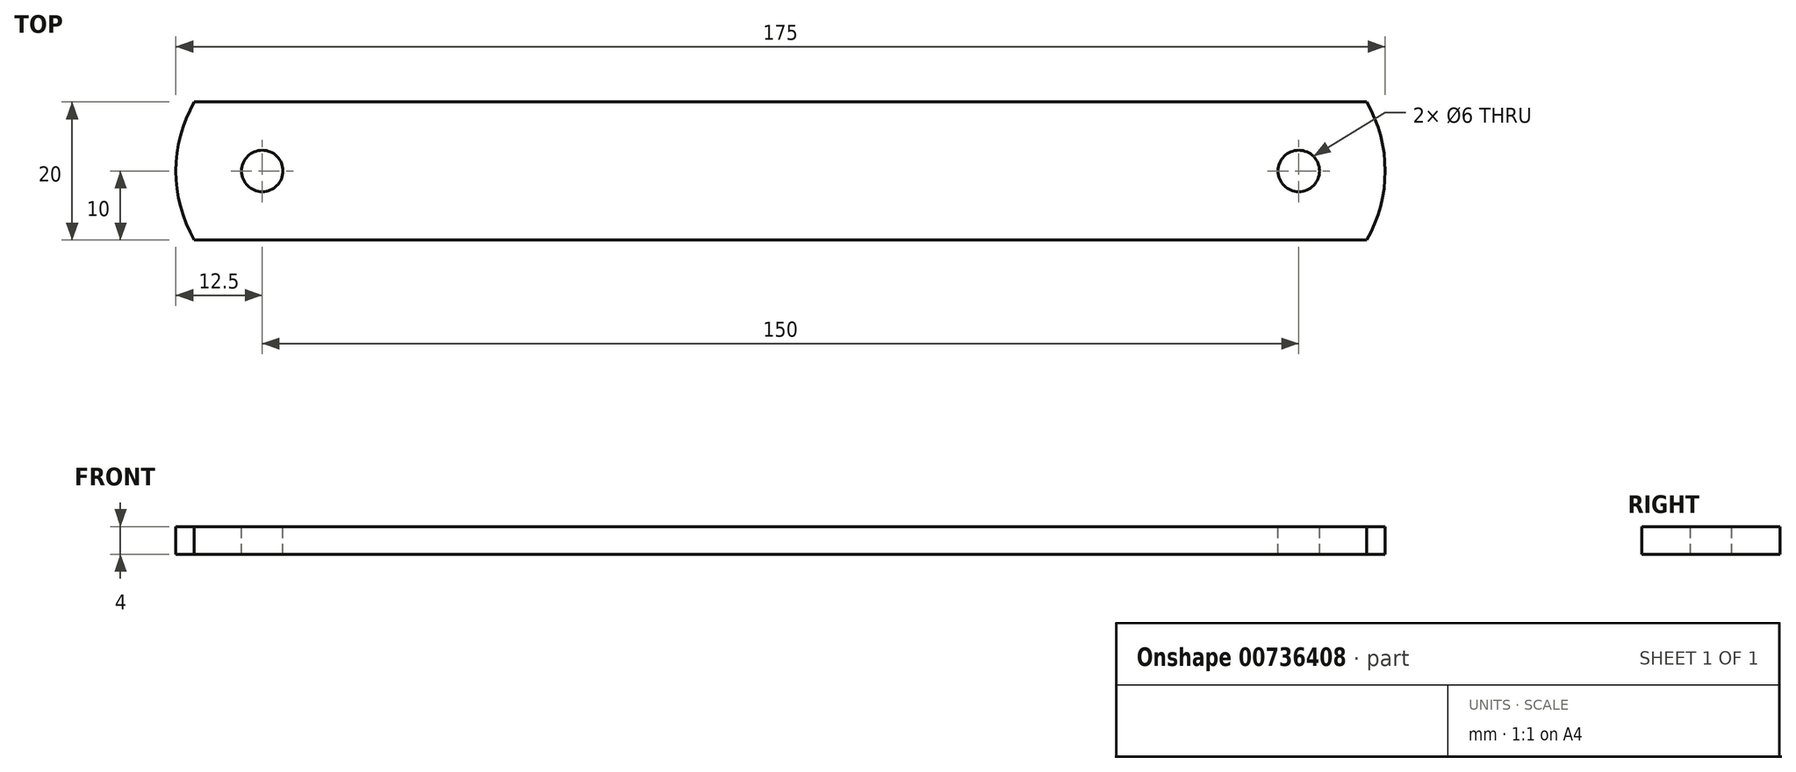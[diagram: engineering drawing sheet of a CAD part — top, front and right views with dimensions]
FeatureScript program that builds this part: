
annotation { "Feature Type Name" : "Feature", "Feature Type Description" : "" }
export const myFeature = defineFeature(function(context is Context, id is Id, definition is map)
    precondition{}
    {
        {
            var Q0;
            Q0=qCreatedBy(makeId("Top.planeOp"),FACE);
            var sketch = newSketch(context, id + "F0", { "sketchPlane" : qUnion([Q0])});
            skLineSegment(sketch, "E0.bottom", {"start": v(0, 0) * mm, "end": v(169.64, 0) * mm});
            skLineSegment(sketch, "E0.top", {"start": v(0, -20) * mm, "end": v(169.64, -20) * mm});
            skArc(sketch, "E1", {"start": v(169.64, -20) * mm, "mid": v(172.32, -10) * mm, "end": v(169.64, 0) * mm});
            skArc(sketch, "E2", {"start": v(0, 0) * mm, "mid": v(-2.68, -10) * mm, "end": v(0, -20) * mm});
            skSolve(sketch);
        }
        {
            var Q0;
            Q0=makeQuery(id+"F0.imprint","IMPRINT",FACE,{"disambiguationData":[TD([[makeQuery(id+"F0.imprint","IMPRINT",EDGE,{"derivedFrom":sQuery(id+"F0.wireOp",EDGE,"E0.bottom")}),-1.0]])]});
            extrude(context, id + "F1", {"entities" : qUnion([Q0]), "depth" : 4 * mm, "offsetDistance" : 25 * mm});
        }
        {
            var Q0;
            Q0=makeQuery(id+"F1.opExtrude","CAP_FACE",FACE,{"disambiguationData":[OSD([sQuery(id+"F0.wireOp",EDGE,"E0.bottom"),sQuery(id+"F0.wireOp",EDGE,"E0.top"),sQuery(id+"F0.wireOp",EDGE,"E1"),sQuery(id+"F0.wireOp",EDGE,"E2")])],"isStart":false});
            var sketch = newSketch(context, id + "F2", { "sketchPlane" : qUnion([Q0])});
            skCircle(sketch, "E3", {"center": v(159.82, -10) * mm, "radius": 3 * mm});
            skCircle(sketch, "E4", {"center": v(9.82, -10) * mm, "radius": 3 * mm});
            skSolve(sketch);
        }
        {
            var Q0;
            Q0=qSketchRegion(id+"F2",true);
            extrude(context, id + "F3", {"entities" : qUnion([Q0]), "operationType" : NewBodyOperationType.REMOVE, "oppositeDirection" : true, "depth" : 4 * mm, "offsetDistance" : 25 * mm});
        }
    });
